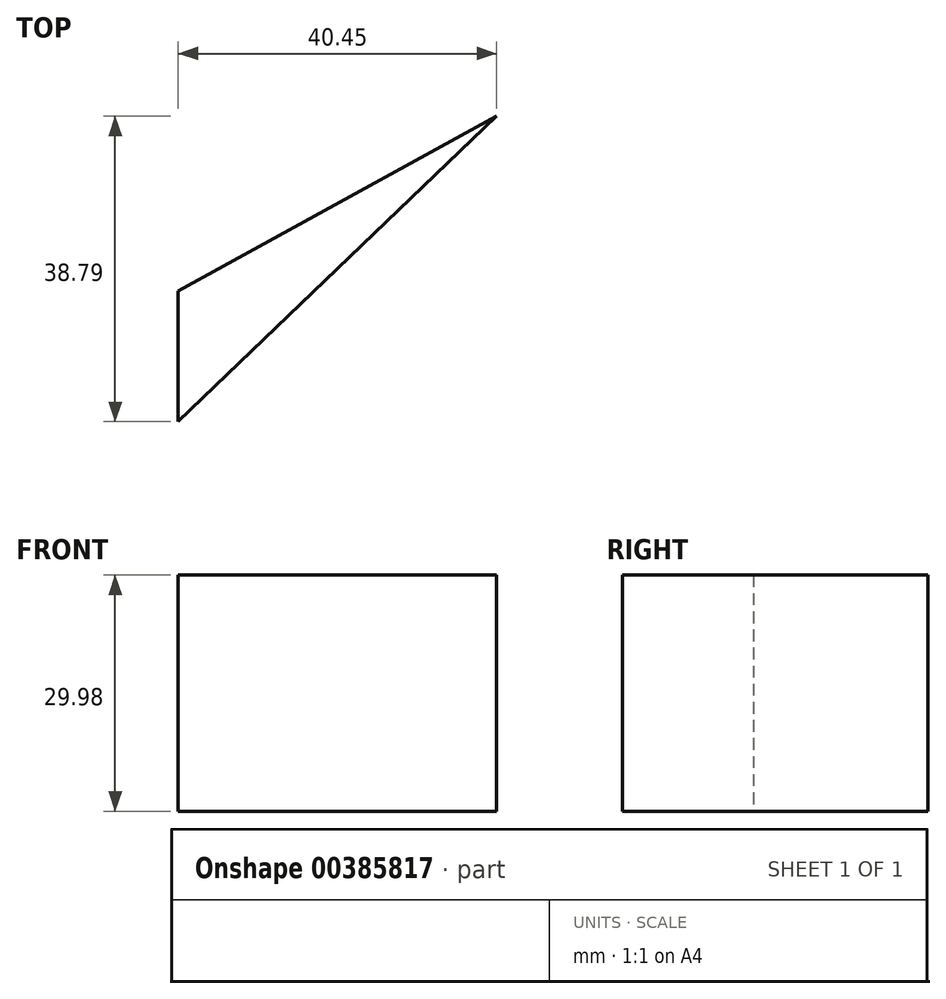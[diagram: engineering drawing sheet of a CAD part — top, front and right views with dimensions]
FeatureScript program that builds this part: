
annotation { "Feature Type Name" : "Feature", "Feature Type Description" : "" }
export const myFeature = defineFeature(function(context is Context, id is Id, definition is map)
    precondition{}
    {
        {
            var Q0;
            Q0=qCreatedBy(makeId("Top.planeOp"),FACE);
            var sketch = newSketch(context, id + "F0", { "sketchPlane" : qUnion([Q0])});
            skLineSegment(sketch, "E0", {"start": v(-26.76, 43.77) * mm, "end": v(-27.18, 39.2) * mm});
            skLineSegment(sketch, "E1", {"start": v(-27.18, 39.2) * mm, "end": v(-7.05, 39.2) * mm});
            skLineSegment(sketch, "E2", {"start": v(-7.05, 39.2) * mm, "end": v(-7.05, 34.44) * mm});
            skLineSegment(sketch, "E3", {"start": v(-7.05, 34.44) * mm, "end": v(-7.05, 39.2) * mm});
            skLineSegment(sketch, "E4", {"start": v(29.87, 14.52) * mm, "end": v(29.87, -20.95) * mm});
            skLineSegment(sketch, "E5", {"start": v(29.87, -20.95) * mm, "end": v(64.1, -20.95) * mm});
            skLineSegment(sketch, "E6", {"start": v(64.1, -20.95) * mm, "end": v(64.1, 19.09) * mm});
            skLineSegment(sketch, "E7", {"start": v(64.1, 19.09) * mm, "end": v(61, 14.73) * mm});
            skLineSegment(sketch, "E8", {"start": v(29.87, 14.52) * mm, "end": v(30.91, 13.28) * mm});
            skLineSegment(sketch, "E9", {"start": v(30.91, 13.28) * mm, "end": v(61, 14.73) * mm});
            skLineSegment(sketch, "E10", {"start": v(-56.01, 0) * mm, "end": v(-46.89, 24.69) * mm});
            skLineSegment(sketch, "E11", {"start": v(-40.45, -22.2) * mm, "end": v(-40.45, -38.8) * mm});
            skLineSegment(sketch, "E12", {"start": v(-40.45, -38.8) * mm, "end": v(0, 0) * mm});
            skLineSegment(sketch, "E13", {"start": v(0, 0) * mm, "end": v(-40.45, -22.2) * mm});
            skLineSegment(sketch, "E14", {"start": v(150.05, 47.77) * mm, "end": v(46.99, 35.35) * mm});
            skLineSegment(sketch, "E15", {"start": v(46.99, 35.35) * mm, "end": v(145.97, 0) * mm});
            skLineSegment(sketch, "E16", {"start": v(150.05, 47.77) * mm, "end": v(-80.17, 34.98) * mm});
            skSolve(sketch);
        }
        {
            var Q0;
            Q0=makeQuery(id+"F0.imprint","IMPRINT",FACE,{"disambiguationData":[TD([[makeQuery(id+"F0.imprint","IMPRINT",EDGE,{"derivedFrom":sQuery(id+"F0.wireOp",EDGE,"E11")}),1.0]])]});
            extrude(context, id + "F1", {"entities" : qUnion([Q0]), "depth" : 29.98 * mm});
        }
    });
